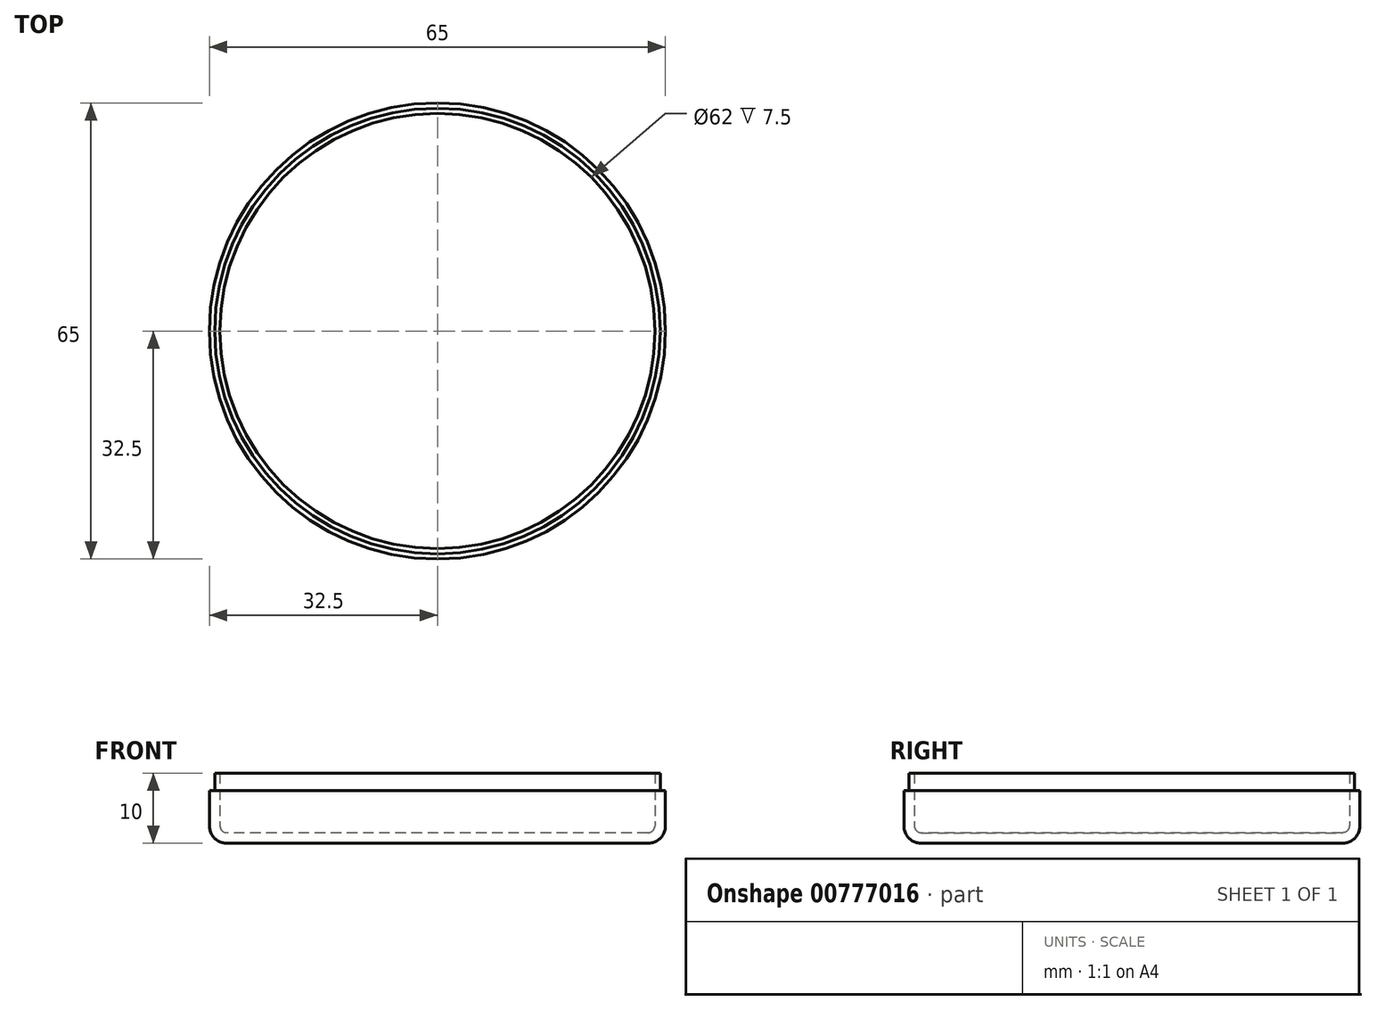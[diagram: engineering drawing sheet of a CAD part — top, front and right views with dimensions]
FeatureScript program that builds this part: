
annotation { "Feature Type Name" : "Feature", "Feature Type Description" : "" }
export const myFeature = defineFeature(function(context is Context, id is Id, definition is map)
    precondition{}
    {
        {
            var Q0;
            Q0=qCreatedBy(makeId("Top.planeOp"),FACE);
            var sketch = newSketch(context, id + "F0", { "sketchPlane" : qUnion([Q0])});
            skCircle(sketch, "E0", {"center": v(0, 0) * mm, "radius": 32.5 * mm});
            skSolve(sketch);
        }
        {
            var Q0;
            Q0=qSketchRegion(id+"F0",true);
            extrude(context, id + "F1", {"entities" : qUnion([Q0]), "depth" : 10 * mm, "offsetDistance" : 25 * mm});
        }
        {
            var Q0;
            Q0=makeQuery(id+"F1.opExtrude","CAP_FACE",FACE,{"disambiguationData":[OSD([sQuery(id+"F0.wireOp",EDGE,"pcHNsLAs-uuIG-92PN-J4nV-sG1yAEwh4vms.bottom"),sQuery(id+"F0.wireOp",EDGE,"pcHNsLAs-uuIG-92PN-J4nV-sG1yAEwh4vms.top"),sQuery(id+"F0.wireOp",EDGE,"pcHNsLAs-uuIG-92PN-J4nV-sG1yAEwh4vms.left"),sQuery(id+"F0.wireOp",EDGE,"pcHNsLAs-uuIG-92PN-J4nV-sG1yAEwh4vms.right"),sQuery(id+"F0.wireOp",EDGE,"3d6bdb04-9177-4708-87b0-630207d0257c.filletArc"),sQuery(id+"F0.wireOp",EDGE,"a6119fb4-ba20-4dce-af5d-a38932c804a4.filletArc"),sQuery(id+"F0.wireOp",EDGE,"7038d429-74eb-4160-9e18-919da026d677.filletArc"),sQuery(id+"F0.wireOp",EDGE,"e058b54d-4a7d-470c-b5c4-87012d02d3e7.filletArc")])],"isStart":true});
            var Q1;
            Q1=makeQuery(id+"F1.opExtrude","CAP_FACE",FACE,{"disambiguationData":[OSD([sQuery(id+"F0.wireOp",EDGE,"E0")])],"isStart":true});
            fillet(context, id + "F2", {"entities" : qUnion([Q0, Q1]), "radius" : 2.5 * mm, "tangentPropagation" : true, "allowEdgeOverflow" : false});
        }
        {
            var Q0;
            Q0=makeQuery(id+"F1.opExtrude","CAP_FACE",FACE,{"disambiguationData":[OSD([sQuery(id+"F0.wireOp",EDGE,"pcHNsLAs-uuIG-92PN-J4nV-sG1yAEwh4vms.bottom"),sQuery(id+"F0.wireOp",EDGE,"pcHNsLAs-uuIG-92PN-J4nV-sG1yAEwh4vms.top"),sQuery(id+"F0.wireOp",EDGE,"pcHNsLAs-uuIG-92PN-J4nV-sG1yAEwh4vms.left"),sQuery(id+"F0.wireOp",EDGE,"pcHNsLAs-uuIG-92PN-J4nV-sG1yAEwh4vms.right"),sQuery(id+"F0.wireOp",EDGE,"3d6bdb04-9177-4708-87b0-630207d0257c.filletArc"),sQuery(id+"F0.wireOp",EDGE,"a6119fb4-ba20-4dce-af5d-a38932c804a4.filletArc"),sQuery(id+"F0.wireOp",EDGE,"7038d429-74eb-4160-9e18-919da026d677.filletArc"),sQuery(id+"F0.wireOp",EDGE,"e058b54d-4a7d-470c-b5c4-87012d02d3e7.filletArc")])],"isStart":false});
            var Q1;
            Q1=makeQuery(id+"F1.opExtrude","CAP_FACE",FACE,{"disambiguationData":[OSD([sQuery(id+"F0.wireOp",EDGE,"E0")])],"isStart":false});
            shell(context, id + "F3", {"entities" : qUnion([Q0, Q1]), "thickness" : 1.5 * mm});
        }
        {
            var Q0;
            Q0=makeQuery(id+"F1.opExtrude","CAP_FACE",FACE,{"disambiguationData":[OSD([sQuery(id+"F0.wireOp",EDGE,"E0")])],"isStart":false});
            var sketch = newSketch(context, id + "F4", { "sketchPlane" : qUnion([Q0])});
            skCircle(sketch, "E1.0", {"center": v(0, 0) * mm, "radius": 32.5 * mm});
            skCircle(sketch, "E2.0", {"center": v(0, 0) * mm, "radius": 31.75 * mm});
            skSolve(sketch);
        }
        {
            var Q0;
            Q0=qSketchRegion(id+"F4",true);
            extrude(context, id + "F5", {"entities" : qUnion([Q0]), "operationType" : NewBodyOperationType.REMOVE, "oppositeDirection" : true, "depth" : 2.5 * mm, "offsetDistance" : 25 * mm});
        }
    });
